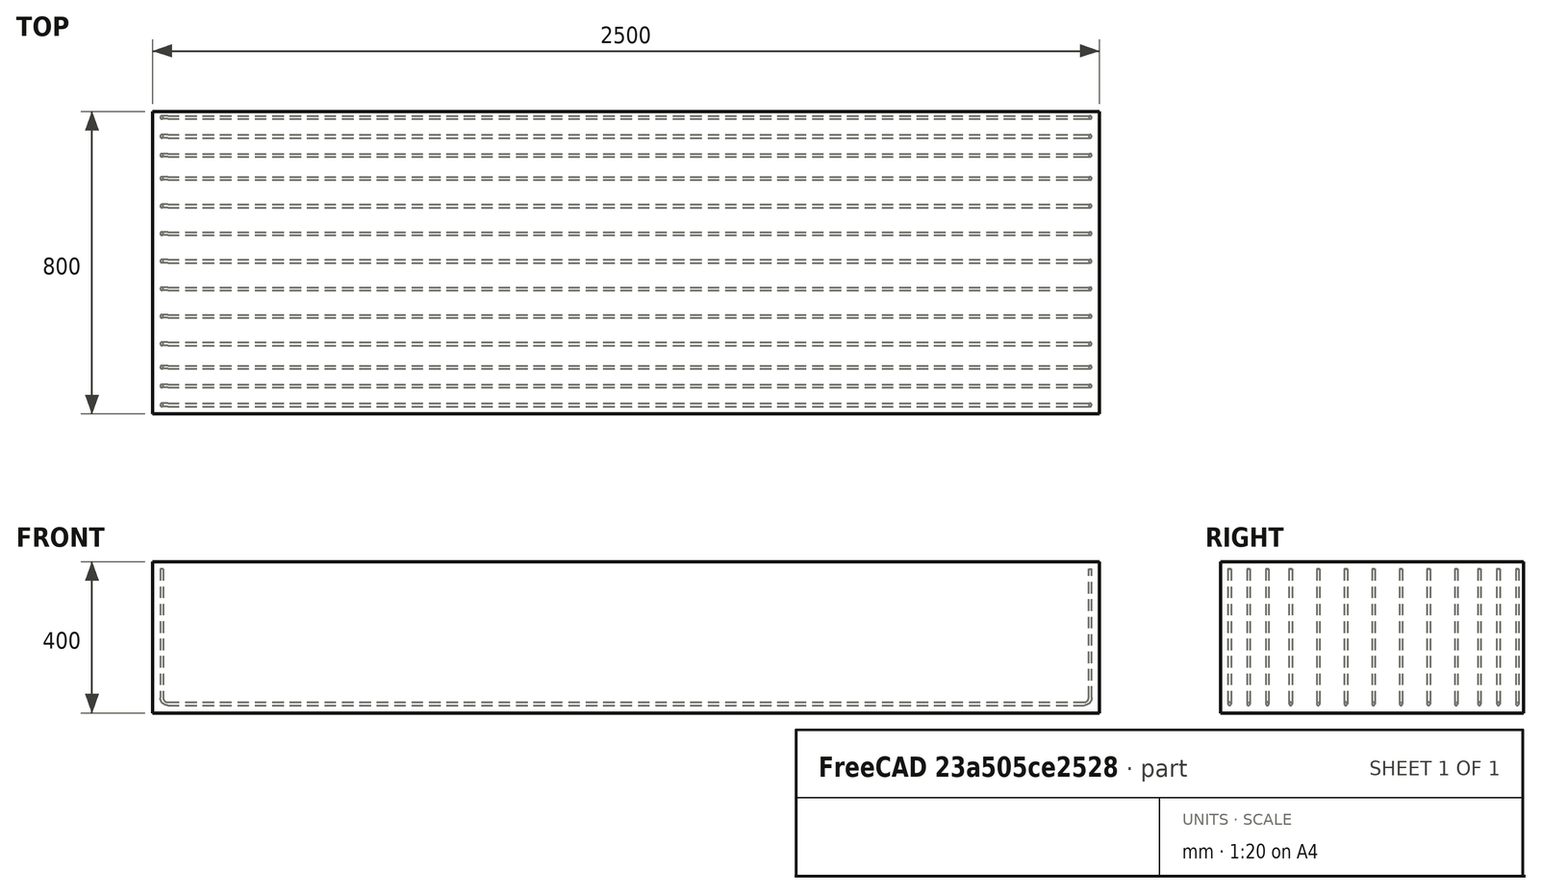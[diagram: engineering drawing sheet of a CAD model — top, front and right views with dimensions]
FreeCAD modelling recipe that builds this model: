
FCSTD DOCUMENT  (FreeCAD 0.19R20802 (Git))
Label: urebar_drawing_dimension
License: All rights reserved
LicenseURL: http://en.wikipedia.org/wiki/All_rights_reserved
objects: TechDraw::DrawViewSymbolPython×12, TechDraw::DrawSVGTemplate×6, TechDraw::DrawPage×6, Part::FeaturePython×2, Sketcher::SketchObject×1
note: 3 computed .brp shape members not serialized (recipe doc carries the construction recipe); baked Part::Feature solids carry a one-line shape summary decoded from their .brp

FEATURE [Part::FeaturePython] Structure  label="Beam"  # Arch/BIM 7 (typed FeaturePython)
  FaceMaker = 0
  Height = 400
  HorizontalArea = 2000000
  IfcData = attributes={"GlobalId": {"name": "GlobalId", "type": "IfcGloballyUniqueId", "is_enum": false, "enum_values": []}, "Description": {"... (+475 chars omitted),+1 more (map truncated)
  IfcType = 7
  Length = 2500
  MoveBase = false
  MoveWithHost = false
  Nodes = (2) [(0,0,-7.77156e-16),(0,0,2500)]
  NodesOffset = 0
  Normal = (0,0,0)
  PerimeterLength = 6600
  Placement = pos=(-1.98245,0.139225,0) rot=(0,0,1;0rad)
  PredefinedType = 0
  VerticalArea = 2640000
  Width = 800
FEATURE [Sketcher::SketchObject] Sketch
  MapMode = 5
  Placement = pos=(-1.98245,-399.861,0) rot=(1,0,0;1.5708rad)
  Support = -> [Structure]
  sketch-geometry (3):
    g0: LineSegment StartX=24 StartY=180 StartZ=0 EndX=24 EndY=-176 EndZ=0
    g1: LineSegment StartX=24 StartY=-176 StartZ=0 EndX=2476 EndY=-176 EndZ=0
    g2: LineSegment StartX=2476 StartY=-176 StartZ=0 EndX=2476 EndY=180 EndZ=0
FEATURE [Part::FeaturePython] Rebar  label="UShapeRebar"  # Arch/BIM 110 (typed FeaturePython)
  Amount = 13
  AmountCheck = false
  Base = -> Sketch
  BottomCover = 20
  CustomSpacing = 3@50.0+7@72.85714285714286+3@50.0
  Diameter = 8
  Direction = (0,0,0)
  Distance = 0
  FrontCover = 20
  HorizontalArea = 0
  Host = -> Structure
  IfcType = 110
  LeftCover = 20
  Length = 3164
  Mark = URb
  MoveBase = false
  MoveWithHost = false
  OffsetEnd = 24
  OffsetStart = 24
  Orientation = Bottom
  PerimeterLength = 0
  PlacementList = 13 placements: [(0,24,-5.32907e-15),(0,74,-1.64313e-14),(0,124,-2.75335e-14),(0,185.429,-4.11734e-14),(0,258.286,-5.73509e-14),(0,331.143,-7.35285e-14),(0,404,-8.9706e-14),(0,476.857,-1.05884e-13),(0,549.714,-1.22061e-13),(0,622.571,-1.38239e-13),(0,684,-1.51879e-13),(0,734,-1.62981e-13),(0,784,-1.74083e-13)]
  RebarShape = 1
  RightCover = 20
  Rounding = 2
  Spacing = 0
  TopCover = 20
  TotalLength = 41132
  TrueSpacing = 50
  VerticalArea = 0
FEATURE [TechDraw::DrawSVGTemplate] Template
  Height = 210
  Orientation = 1
  Width = 297
FEATURE [TechDraw::DrawViewSymbolPython] ReinforcementDrawingView  label="Front View"  # drawing view (typed FeaturePython)
  DimensionBottomOffset = 16
  DimensionLeftOffset = 10
  DimensionRightOffset = 10
  DimensionTopOffset = 10
  Height = 400
  LeftOffset = 20
  LockPosition = false
  MaxHeight = 210
  MaxWidth = 297
  MinBottomOffset = 20
  MinRightOffset = 20
  PositionType = 0
  Rebars = -> [Rebar]
  RebarsColorStyle = 0
  RebarsStrokeWidth = 0.35
  Rotation = 0
  Scale = 0.1028
  ScaleType = 1
  Structure = -> Structure
  StructureColorStyle = 0
  StructureStrokeWidth = 0.5
  Symbol = <blob: 3442 chars omitted>
  Template = -> Template
  TopOffset = 84.44
  View = 0
  VisibleRebars = -> [Rebar]
  Width = 2500
  X = 148.5
  Y = 105
  expr: TopOffset = .Template.Height.Value / 2 - .Height.Value * .Scale / 2
  expr: LeftOffset = .Template.Width.Value / 2 - .Width.Value * .Scale / 2
FEATURE [TechDraw::DrawViewSymbolPython] ReinforcementDimensioning  # drawing view (typed FeaturePython)
  DimensionBottomOffset = 10
  DimensionFormat = %M %C⌀%D,span=%S
  DimensionLeftOffset = 10
  DimensionRightOffset = 10
  DimensionTopOffset = 10
  Font = DejaVu Sans
  FontSize = 3
  LineEndSymbol = 0
  LineMidPointSymbol = 1
  LineStartSymbol = 3
  LineStyle = 0
  LockPosition = false
  MultiRebar_LineEndSymbol = 0
  MultiRebar_LineStartSymbol = 0
  MultiRebar_OuterDimension = true
  MultiRebar_TextPositionType = 0
  ParentDrawingView = -> ReinforcementDrawingView
  Rebar = -> Rebar
  Rotation = 0
  Scale = 0.1028
  ScaleType = 2
  SingleRebar_LineEndSymbol = 0
  SingleRebar_LineStartSymbol = 3
  SingleRebar_OuterDimension = false
  SingleRebar_TextPositionType = 1
  StrokeWidth = 0.25
  Symbol = <svg version="1.1" xmlns="http://www.w3.org/2000/svg" xmlns:xlink="http://www.w3.org/1999/xlink" xmlns:freecad="http://www.freecadweb.org/wiki/index.php?title=Svg_Namespace" width="2500.0mm" height="400.0mm" viewBox="0 0 2500.0 400.0"><g transform="translate(1.982445478439331, 200.00000000000057)"><g><path d="M1922.0 297.2762645914397 L1922.0 175.99999999999972" style="stroke:#00007f;stroke-width:2.431906614785992;stroke-linecap:round;fill:none;" stroke-dasharray="" /><g id="line_mid_points" /><path d="M0,0 -8,-1.5 V1.5 L0,0" style="stroke:#00007f;fill:#00007f;stroke-width:2.431906614785992;stroke-linecap:round;stroke-linejoin:bevel;" transform="translate(1922.0 175.99999999999972) rotate(-90.0 0 0)" /></g><text x="1922.0" y="311.8677042801557" style="white-space:pre;" fill="#005400" font-family="DejaVu Sans" font-size="29.182879377431906" text-anchor="middle" dominant-baseline="baseline" xml:space="preserve">URb 13⌀8,span=760</text></g></svg>
  TextPositionType = 0
  WayPoints = (2) [(0,0,0),(50,0,0)]
  WayPointsType = 0
  X = 148.5
  Y = 105
FEATURE [TechDraw::DrawPage] TechDraw__DrawPage  label="Beam Drawing"
  KeepUpdated = true
  NextBalloonIndex = 1
  ProjectionType = 0
  Template = -> Template
  Views = -> [ReinforcementDrawingView,ReinforcementDimensioning]
FEATURE [TechDraw::DrawSVGTemplate] Template001
  Height = 210
  Orientation = 1
  Width = 297
FEATURE [TechDraw::DrawViewSymbolPython] ReinforcementDrawingView001  label="Rear View"  # drawing view (typed FeaturePython)
  DimensionBottomOffset = 16
  DimensionLeftOffset = 10
  DimensionRightOffset = 10
  DimensionTopOffset = 10
  Height = 400
  LeftOffset = 20
  LockPosition = false
  MaxHeight = 210
  MaxWidth = 297
  MinBottomOffset = 20
  MinRightOffset = 20
  PositionType = 0
  Rebars = -> [Rebar]
  RebarsColorStyle = 0
  RebarsStrokeWidth = 0.35
  Rotation = 0
  Scale = 0.1028
  ScaleType = 1
  Structure = -> Structure
  StructureColorStyle = 0
  StructureStrokeWidth = 0.5
  Symbol = <blob: 3451 chars omitted>
  Template = -> Template001
  TopOffset = 84.44
  View = 1
  VisibleRebars = -> [Rebar]
  Width = 2500
  X = 148.5
  Y = 105
  expr: TopOffset = .Template.Height.Value / 2 - .Height.Value * .Scale / 2
  expr: LeftOffset = .Template.Width.Value / 2 - .Width.Value * .Scale / 2
FEATURE [TechDraw::DrawViewSymbolPython] ReinforcementDimensioning001  # drawing view (typed FeaturePython)
  DimensionBottomOffset = 10
  DimensionFormat = %M %C⌀%D,span=%S
  DimensionLeftOffset = 10
  DimensionRightOffset = 10
  DimensionTopOffset = 10
  Font = DejaVu Sans
  FontSize = 3
  LineEndSymbol = 0
  LineMidPointSymbol = 1
  LineStartSymbol = 3
  LineStyle = 0
  LockPosition = false
  MultiRebar_LineEndSymbol = 0
  MultiRebar_LineStartSymbol = 0
  MultiRebar_OuterDimension = true
  MultiRebar_TextPositionType = 0
  ParentDrawingView = -> ReinforcementDrawingView001
  Rebar = -> Rebar
  Rotation = 0
  Scale = 0.1028
  ScaleType = 2
  SingleRebar_LineEndSymbol = 0
  SingleRebar_LineStartSymbol = 3
  SingleRebar_OuterDimension = false
  SingleRebar_TextPositionType = 1
  StrokeWidth = 0.25
  Symbol = <svg version="1.1" xmlns="http://www.w3.org/2000/svg" xmlns:xlink="http://www.w3.org/1999/xlink" xmlns:freecad="http://www.freecadweb.org/wiki/index.php?title=Svg_Namespace" width="2500.0mm" height="400.0mm" viewBox="0 0 2500.0 400.0"><g transform="translate(2498.0175545215607, 200.00000000000057)"><g><path d="M-264.0 297.2762645914397 L-264.0 175.99999999999972" style="stroke:#00007f;stroke-width:2.431906614785992;stroke-linecap:round;fill:none;" stroke-dasharray="" /><g id="line_mid_points" /><path d="M0,0 -8,-1.5 V1.5 L0,0" style="stroke:#00007f;fill:#00007f;stroke-width:2.431906614785992;stroke-linecap:round;stroke-linejoin:bevel;" transform="translate(-264.0 175.99999999999972) rotate(-90.0 0 0)" /></g><text x="-264.0" y="311.8677042801557" style="white-space:pre;" fill="#005400" font-family="DejaVu Sans" font-size="29.182879377431906" text-anchor="middle" dominant-baseline="baseline" xml:space="preserve">URb 13⌀8,span=760</text></g></svg>
  TextPositionType = 0
  WayPoints = (2) [(0,0,0),(50,0,0)]
  WayPointsType = 0
  X = 148.5
  Y = 105
FEATURE [TechDraw::DrawPage] TechDraw__DrawPage001  label="Beam Drawing001"
  KeepUpdated = true
  NextBalloonIndex = 1
  ProjectionType = 0
  Template = -> Template001
  Views = -> [ReinforcementDrawingView001,ReinforcementDimensioning001]
FEATURE [TechDraw::DrawSVGTemplate] Template002
  Height = 210
  Orientation = 1
  Width = 297
FEATURE [TechDraw::DrawViewSymbolPython] ReinforcementDrawingView002  label="Left View"  # drawing view (typed FeaturePython)
  DimensionBottomOffset = 10
  DimensionLeftOffset = 10
  DimensionRightOffset = 10
  DimensionTopOffset = 16
  Height = 400
  LeftOffset = 20
  LockPosition = false
  MaxHeight = 210
  MaxWidth = 297
  MinBottomOffset = 20
  MinRightOffset = 20
  PositionType = 0
  Rebars = -> [Rebar]
  RebarsColorStyle = 0
  RebarsStrokeWidth = 0.35
  Rotation = 0
  Scale = 0.32125
  ScaleType = 1
  Structure = -> Structure
  StructureColorStyle = 0
  StructureStrokeWidth = 0.5
  Symbol = <blob: 9858 chars omitted>
  Template = -> Template002
  TopOffset = 40.75
  View = 2
  VisibleRebars = -> [Rebar]
  Width = 800
  X = 148.5
  Y = 105
  expr: TopOffset = .Template.Height.Value / 2 - .Height.Value * .Scale / 2
  expr: LeftOffset = .Template.Width.Value / 2 - .Width.Value * .Scale / 2
FEATURE [TechDraw::DrawViewSymbolPython] ReinforcementDimensioning002  # drawing view (typed FeaturePython)
  DimensionBottomOffset = 10
  DimensionFormat = %M %C⌀%D,span=%S
  DimensionLeftOffset = 10
  DimensionRightOffset = 10
  DimensionTopOffset = 10
  Font = DejaVu Sans
  FontSize = 3
  LineEndSymbol = 0
  LineMidPointSymbol = 1
  LineStartSymbol = 3
  LineStyle = 0
  LockPosition = false
  MultiRebar_LineEndSymbol = 0
  MultiRebar_LineStartSymbol = 0
  MultiRebar_OuterDimension = true
  MultiRebar_TextPositionType = 0
  ParentDrawingView = -> ReinforcementDrawingView002
  Rebar = -> Rebar
  Rotation = 0
  Scale = 0.32125
  ScaleType = 2
  SingleRebar_LineEndSymbol = 0
  SingleRebar_LineStartSymbol = 3
  SingleRebar_OuterDimension = false
  SingleRebar_TextPositionType = 1
  StrokeWidth = 0.25
  Symbol = <blob: 5757 chars omitted>
  TextPositionType = 0
  WayPoints = (2) [(0,0,0),(50,0,0)]
  WayPointsType = 0
  X = 148.5
  Y = 105
FEATURE [TechDraw::DrawPage] TechDraw__DrawPage002  label="Beam Drawing002"
  KeepUpdated = true
  NextBalloonIndex = 1
  ProjectionType = 0
  Template = -> Template002
  Views = -> [ReinforcementDrawingView002,ReinforcementDimensioning002]
FEATURE [TechDraw::DrawSVGTemplate] Template003
  Height = 210
  Orientation = 1
  Width = 297
FEATURE [TechDraw::DrawViewSymbolPython] ReinforcementDrawingView003  label="Right View"  # drawing view (typed FeaturePython)
  DimensionBottomOffset = 10
  DimensionLeftOffset = 10
  DimensionRightOffset = 10
  DimensionTopOffset = 16
  Height = 400
  LeftOffset = 20
  LockPosition = false
  MaxHeight = 210
  MaxWidth = 297
  MinBottomOffset = 20
  MinRightOffset = 20
  PositionType = 0
  Rebars = -> [Rebar]
  RebarsColorStyle = 0
  RebarsStrokeWidth = 0.35
  Rotation = 0
  Scale = 0.32125
  ScaleType = 1
  Structure = -> Structure
  StructureColorStyle = 0
  StructureStrokeWidth = 0.5
  Symbol = <blob: 9849 chars omitted>
  Template = -> Template003
  TopOffset = 40.75
  View = 3
  VisibleRebars = -> [Rebar]
  Width = 800
  X = 148.5
  Y = 105
  expr: TopOffset = .Template.Height.Value / 2 - .Height.Value * .Scale / 2
  expr: LeftOffset = .Template.Width.Value / 2 - .Width.Value * .Scale / 2
FEATURE [TechDraw::DrawViewSymbolPython] ReinforcementDimensioning003  # drawing view (typed FeaturePython)
  DimensionBottomOffset = 10
  DimensionFormat = %M %C⌀%D,span=%S
  DimensionLeftOffset = 10
  DimensionRightOffset = 10
  DimensionTopOffset = 10
  Font = DejaVu Sans
  FontSize = 3
  LineEndSymbol = 0
  LineMidPointSymbol = 1
  LineStartSymbol = 3
  LineStyle = 0
  LockPosition = false
  MultiRebar_LineEndSymbol = 0
  MultiRebar_LineStartSymbol = 0
  MultiRebar_OuterDimension = true
  MultiRebar_TextPositionType = 0
  ParentDrawingView = -> ReinforcementDrawingView003
  Rebar = -> Rebar
  Rotation = 0
  Scale = 0.32125
  ScaleType = 2
  SingleRebar_LineEndSymbol = 0
  SingleRebar_LineStartSymbol = 3
  SingleRebar_OuterDimension = false
  SingleRebar_TextPositionType = 1
  StrokeWidth = 0.25
  Symbol = <blob: 5730 chars omitted>
  TextPositionType = 0
  WayPoints = (2) [(0,0,0),(50,0,0)]
  WayPointsType = 0
  X = 148.5
  Y = 105
FEATURE [TechDraw::DrawPage] TechDraw__DrawPage003  label="Beam Drawing003"
  KeepUpdated = true
  NextBalloonIndex = 1
  ProjectionType = 0
  Template = -> Template003
  Views = -> [ReinforcementDrawingView003,ReinforcementDimensioning003]
FEATURE [TechDraw::DrawSVGTemplate] Template004
  Height = 210
  Orientation = 1
  Width = 297
FEATURE [TechDraw::DrawViewSymbolPython] ReinforcementDrawingView004  label="Top View"  # drawing view (typed FeaturePython)
  DimensionBottomOffset = 10
  DimensionLeftOffset = 10
  DimensionRightOffset = 16
  DimensionTopOffset = 10
  Height = 800
  LeftOffset = 20
  LockPosition = false
  MaxHeight = 210
  MaxWidth = 297
  MinBottomOffset = 20
  MinRightOffset = 20
  PositionType = 0
  Rebars = -> [Rebar]
  RebarsColorStyle = 0
  RebarsStrokeWidth = 0.35
  Rotation = 0
  Scale = 0.1028
  ScaleType = 1
  Structure = -> Structure
  StructureColorStyle = 0
  StructureStrokeWidth = 0.5
  Symbol = <blob: 9308 chars omitted>
  Template = -> Template004
  TopOffset = 63.88
  View = 4
  VisibleRebars = -> [Rebar]
  Width = 2500
  X = 148.5
  Y = 105
  expr: TopOffset = .Template.Height.Value / 2 - .Height.Value * .Scale / 2
  expr: LeftOffset = .Template.Width.Value / 2 - .Width.Value * .Scale / 2
FEATURE [TechDraw::DrawViewSymbolPython] ReinforcementDimensioning004  # drawing view (typed FeaturePython)
  DimensionBottomOffset = 10
  DimensionFormat = %M %C⌀%D,span=%S
  DimensionLeftOffset = 10
  DimensionRightOffset = 10
  DimensionTopOffset = 10
  Font = DejaVu Sans
  FontSize = 3
  LineEndSymbol = 0
  LineMidPointSymbol = 1
  LineStartSymbol = 3
  LineStyle = 0
  LockPosition = false
  MultiRebar_LineEndSymbol = 0
  MultiRebar_LineStartSymbol = 0
  MultiRebar_OuterDimension = true
  MultiRebar_TextPositionType = 0
  ParentDrawingView = -> ReinforcementDrawingView004
  Rebar = -> Rebar
  Rotation = 0
  Scale = 0.1028
  ScaleType = 2
  SingleRebar_LineEndSymbol = 0
  SingleRebar_LineStartSymbol = 3
  SingleRebar_OuterDimension = false
  SingleRebar_TextPositionType = 1
  StrokeWidth = 0.25
  Symbol = <blob: 5575 chars omitted>
  TextPositionType = 0
  WayPoints = (2) [(0,0,0),(50,0,0)]
  WayPointsType = 0
  X = 148.5
  Y = 105
FEATURE [TechDraw::DrawPage] TechDraw__DrawPage004  label="Beam Drawing004"
  KeepUpdated = true
  NextBalloonIndex = 1
  ProjectionType = 0
  Template = -> Template004
  Views = -> [ReinforcementDrawingView004,ReinforcementDimensioning004]
FEATURE [TechDraw::DrawSVGTemplate] Template005
  Height = 210
  Orientation = 1
  Width = 297
FEATURE [TechDraw::DrawViewSymbolPython] ReinforcementDrawingView005  label="Bottom View"  # drawing view (typed FeaturePython)
  DimensionBottomOffset = 10
  DimensionLeftOffset = 10
  DimensionRightOffset = 16
  DimensionTopOffset = 10
  Height = 800
  LeftOffset = 20
  LockPosition = false
  MaxHeight = 210
  MaxWidth = 297
  MinBottomOffset = 20
  MinRightOffset = 20
  PositionType = 0
  Rebars = -> [Rebar]
  RebarsColorStyle = 0
  RebarsStrokeWidth = 0.35
  Rotation = 0
  Scale = 0.1028
  ScaleType = 1
  Structure = -> Structure
  StructureColorStyle = 0
  StructureStrokeWidth = 0.5
  Symbol = <blob: 9300 chars omitted>
  Template = -> Template005
  TopOffset = 63.88
  View = 5
  VisibleRebars = -> [Rebar]
  Width = 2500
  X = 148.5
  Y = 105
  expr: TopOffset = .Template.Height.Value / 2 - .Height.Value * .Scale / 2
  expr: LeftOffset = .Template.Width.Value / 2 - .Width.Value * .Scale / 2
FEATURE [TechDraw::DrawViewSymbolPython] ReinforcementDimensioning005  # drawing view (typed FeaturePython)
  DimensionBottomOffset = 10
  DimensionFormat = %M %C⌀%D,span=%S
  DimensionLeftOffset = 10
  DimensionRightOffset = 10
  DimensionTopOffset = 10
  Font = DejaVu Sans
  FontSize = 3
  LineEndSymbol = 0
  LineMidPointSymbol = 1
  LineStartSymbol = 3
  LineStyle = 0
  LockPosition = false
  MultiRebar_LineEndSymbol = 0
  MultiRebar_LineStartSymbol = 0
  MultiRebar_OuterDimension = true
  MultiRebar_TextPositionType = 0
  ParentDrawingView = -> ReinforcementDrawingView005
  Rebar = -> Rebar
  Rotation = 0
  Scale = 0.1028
  ScaleType = 2
  SingleRebar_LineEndSymbol = 0
  SingleRebar_LineStartSymbol = 3
  SingleRebar_OuterDimension = false
  SingleRebar_TextPositionType = 1
  StrokeWidth = 0.25
  Symbol = <blob: 5559 chars omitted>
  TextPositionType = 0
  WayPoints = (2) [(0,0,0),(50,0,0)]
  WayPointsType = 0
  X = 148.5
  Y = 105
FEATURE [TechDraw::DrawPage] TechDraw__DrawPage005  label="Beam Drawing005"
  KeepUpdated = true
  NextBalloonIndex = 1
  ProjectionType = 0
  Template = -> Template005
  Views = -> [ReinforcementDrawingView005,ReinforcementDimensioning005]
